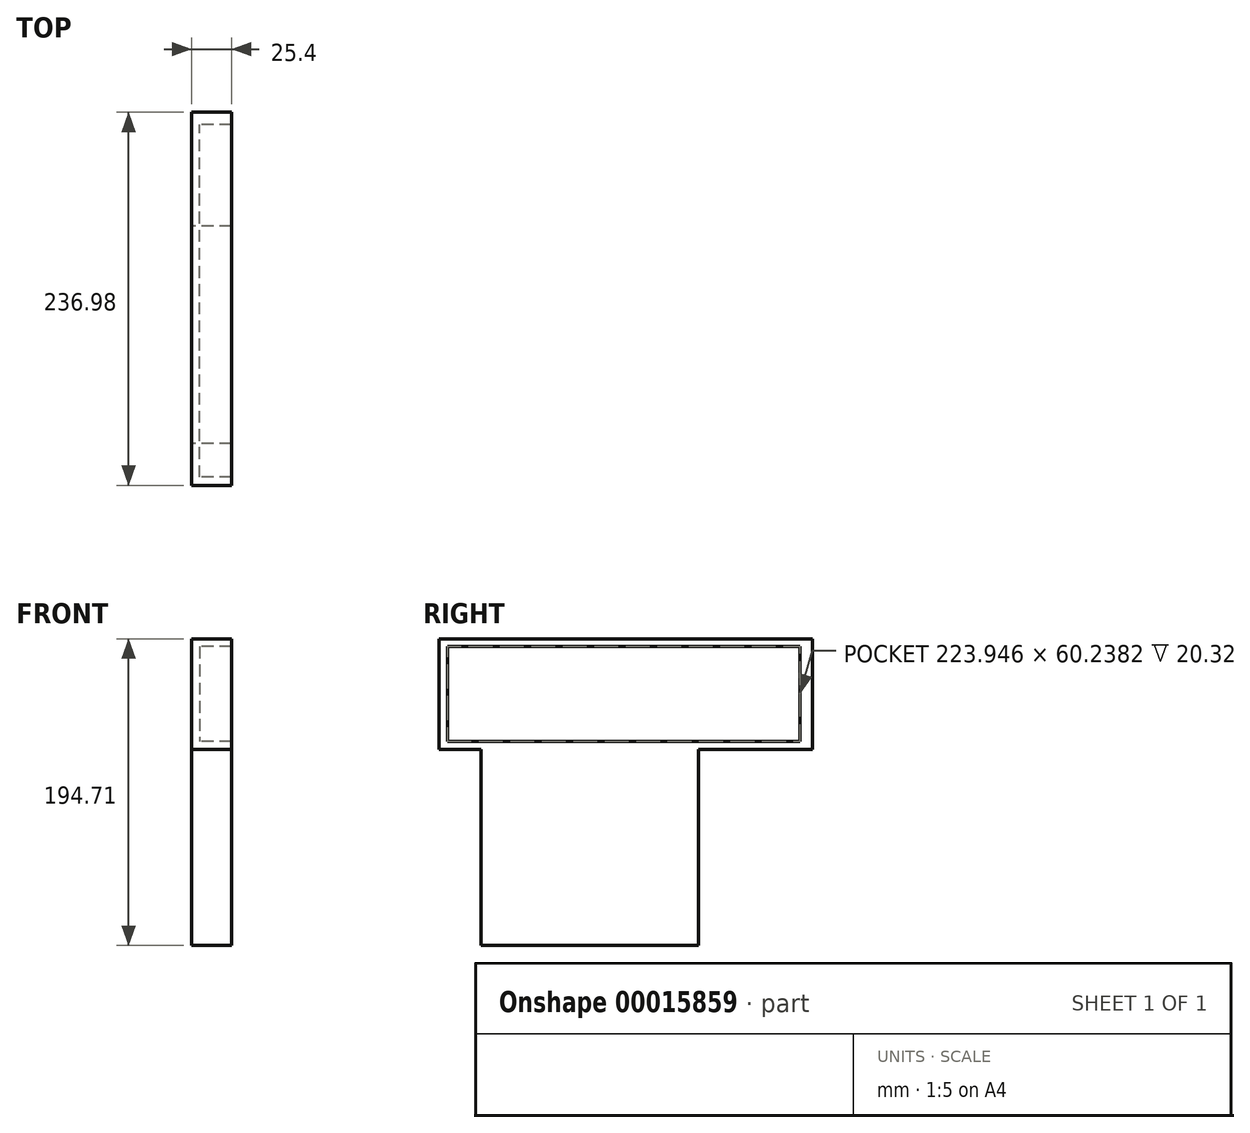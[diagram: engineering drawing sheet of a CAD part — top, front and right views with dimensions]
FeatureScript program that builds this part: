
annotation { "Feature Type Name" : "Feature", "Feature Type Description" : "" }
export const myFeature = defineFeature(function(context is Context, id is Id, definition is map)
    precondition{}
    {
        {
            var Q0;
            Q0=qCreatedBy(makeId("Right.planeOp"),FACE);
            var sketch = newSketch(context, id + "F0", { "sketchPlane" : qUnion([Q0])});
            skLineSegment(sketch, "E0.bottom", {"start": v(43.5, 0) * mm, "end": v(-94.59, 0) * mm});
            skLineSegment(sketch, "E0.top", {"start": v(43.5, -124.57) * mm, "end": v(-94.59, -124.57) * mm});
            skLineSegment(sketch, "E0.left", {"start": v(43.5, 0) * mm, "end": v(43.5, -124.57) * mm});
            skLineSegment(sketch, "E0.right", {"start": v(-94.59, 0) * mm, "end": v(-94.59, -124.57) * mm});
            skLineSegment(sketch, "E1.bottom", {"start": v(-121.1, 70.14) * mm, "end": v(115.89, 70.14) * mm});
            skLineSegment(sketch, "E1.top", {"start": v(-121.1, 0) * mm, "end": v(115.89, 0) * mm});
            skLineSegment(sketch, "E1.left", {"start": v(-121.1, 70.14) * mm, "end": v(-121.1, 0) * mm});
            skLineSegment(sketch, "E1.right", {"start": v(115.89, 70.14) * mm, "end": v(115.89, 0) * mm});
            skLineSegment(sketch, "E2.bottom", {"start": v(-115.85, 65.21) * mm, "end": v(108.1, 65.21) * mm});
            skLineSegment(sketch, "E2.top", {"start": v(-115.85, 4.97) * mm, "end": v(108.1, 4.97) * mm});
            skLineSegment(sketch, "E2.left", {"start": v(-115.85, 65.21) * mm, "end": v(-115.85, 4.97) * mm});
            skLineSegment(sketch, "E2.right", {"start": v(108.1, 65.21) * mm, "end": v(108.1, 4.97) * mm});
            skSolve(sketch);
        }
        {
            var Q0;
            Q0=makeQuery(id+"F0.imprint","IMPRINT",FACE,{"disambiguationData":[TD([[makeQuery(id+"F0.imprint","IMPRINT",EDGE,{"derivedFrom":sQuery(id+"F0.wireOp",EDGE,"E0.top")}),-1.0]])]});
            var Q1;
            Q1=makeQuery(id+"F0.imprint","IMPRINT",FACE,{"disambiguationData":[TD([[makeQuery(id+"F0.imprint","IMPRINT",EDGE,{"derivedFrom":sQuery(id+"F0.wireOp",EDGE,"E1.bottom")}),-1.0]])]});
            extrude(context, id + "F1", {"entities" : qUnion([Q0, Q1]), "depth" : 25.4 * mm});
        }
        {
            var Q0;
            Q0=makeQuery(id+"F0.imprint","IMPRINT",FACE,{"disambiguationData":[TD([[makeQuery(id+"F0.imprint","IMPRINT",EDGE,{"derivedFrom":sQuery(id+"F0.wireOp",EDGE,"E2.bottom")}),-1.0]])]});
            extrude(context, id + "F2", {"entities" : qUnion([Q0]), "operationType" : NewBodyOperationType.ADD, "depth" : 5.08 * mm});
        }
    });
